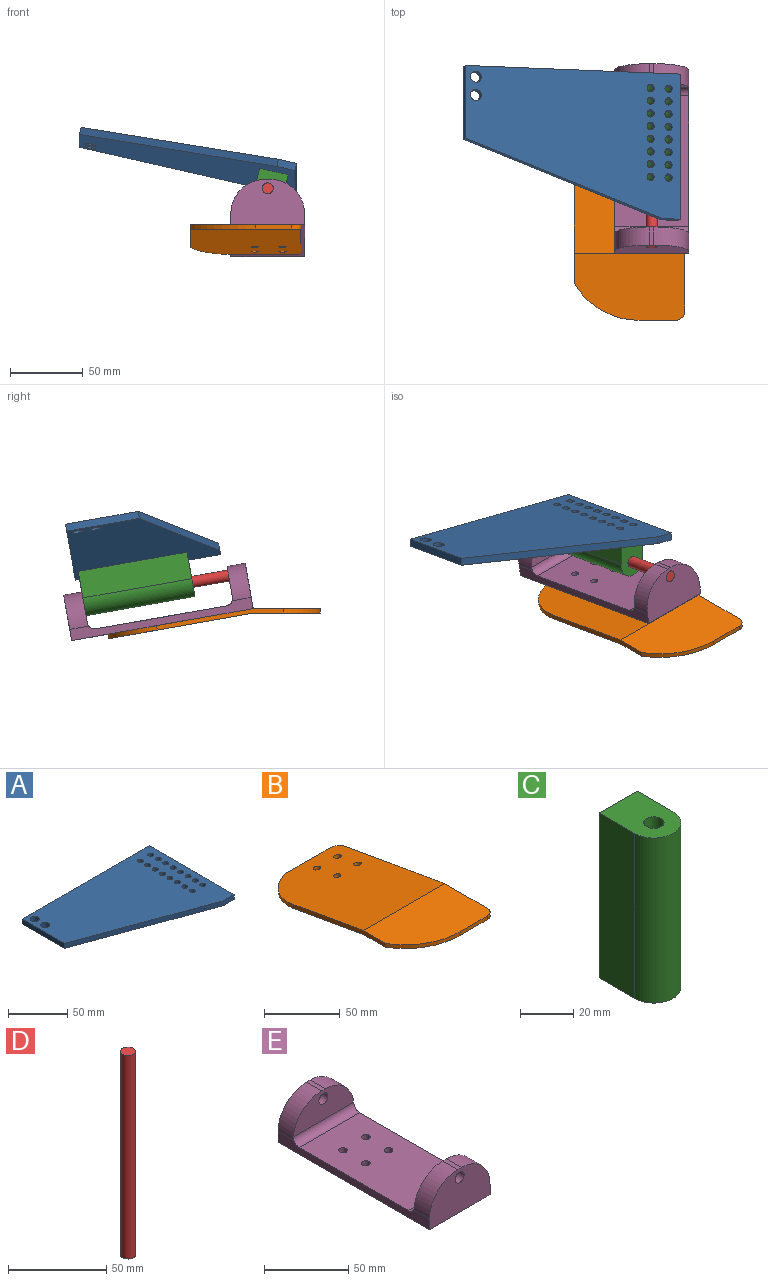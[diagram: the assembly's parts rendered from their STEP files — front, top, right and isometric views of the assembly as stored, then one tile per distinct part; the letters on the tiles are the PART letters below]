
ASSEMBLY  parts=5 mates=8
PART A: 25 faces, bbox 152.4x101.6x5.1 mm
  f0: plane 101.6x5.08mm, normal (1,0,0), area 516.1mm2, adj f1,f20,f22,f23
  f1: plane 152.4x5.08mm, normal (0,1,0), area 774.2mm2, adj f0,f2,f22,f23
  f2: plane 50.8x5.08mm, normal (-1,0,0), area 258.1mm2, adj f1,f22,f23,f24
  f3: cylinder r=3.81mm len=7.62mm, axis (0,0,-1), area 121.6mm2, adj f22,f23
  f4: cylinder r=2.54mm len=5.08mm, axis (0,0,-1), area 81.1mm2, adj f22,f23
  f5: cylinder r=2.54mm len=5.08mm, axis (0,0,-1), area 81.1mm2, adj f22,f23
  f6: cylinder r=2.54mm len=5.08mm, axis (0,0,-1), area 81.1mm2, adj f22,f23
  f7: cylinder r=2.54mm len=5.08mm, axis (0,0,-1), area 81.1mm2, adj f22,f23
  f8: cylinder r=2.54mm len=5.08mm, axis (0,0,-1), area 81.1mm2, adj f22,f23
  f9: cylinder r=2.54mm len=5.08mm, axis (0,0,-1), area 81.1mm2, adj f22,f23
  f10: cylinder r=2.54mm len=5.08mm, axis (0,0,-1), area 81.1mm2, adj f22,f23
  f11: cylinder r=2.54mm len=5.08mm, axis (0,0,-1), area 81.1mm2, adj f22,f23
  f12: cylinder r=2.54mm len=5.08mm, axis (0,0,-1), area 81.1mm2, adj f22,f23
  f13: cylinder r=2.54mm len=5.08mm, axis (0,0,-1), area 81.1mm2, adj f22,f23
  f14: cylinder r=2.54mm len=5.08mm, axis (0,0,-1), area 81.1mm2, adj f22,f23
  f15: cylinder r=2.54mm len=5.08mm, axis (0,0,-1), area 81.1mm2, adj f22,f23
  f16: cylinder r=2.54mm len=5.08mm, axis (0,0,-1), area 81.1mm2, adj f22,f23
  f17: cylinder r=2.54mm len=5.08mm, axis (0,0,-1), area 81.1mm2, adj f22,f23
  f18: cylinder r=2.54mm len=5.08mm, axis (0,0,-1), area 81.1mm2, adj f22,f23
  f19: cylinder r=2.54mm len=5.08mm, axis (0,0,-1), area 81.1mm2, adj f22,f23
  f20: plane 12.83x5.08mm, normal (0,-1,0), area 65.2mm2, adj f0,f22,f23,f24
  f21: cylinder r=3.81mm len=7.62mm, axis (0,0,-1), area 121.6mm2, adj f22,f23
  f22: plane 152.4x101.6mm, normal (0,0,1), area 11523.2mm2, adj f0,f1,f2,f3,f4,f5,f6,f7
  f23: plane 152.4x101.6mm, normal (0,0,-1), area 11523.2mm2, adj f0,f1,f2,f3,f4,f5,f6,f7
  f24: plane 139.57x50.8mm, normal (-0.34,-0.94,0), area 754.5mm2, adj f2,f20,f22,f23
PART B: 16 faces, bbox 76.2x146.3x20.7 mm
  f0: plane 42.15x3.05mm, normal (0,0.98,-0.17), area 130.4mm2, adj f1,f2,f13,f14
  f1: plane 100.06x76.2mm, normal (0,-0.17,-0.98), area 7396.1mm2, adj f0,f3,f4,f8,f9,f10,f11,f12
  f2: plane 100.06x76.2mm, normal (0,0.17,0.98), area 7396.1mm2, adj f0,f3,f4,f7,f9,f10,f11,f12
  f3: plane 133.71x19.59mm, normal (1,0,0), area 415.6mm2, adj f1,f2,f7,f8,f14,f15
  f4: plane 87.48x14.8mm, normal (-1,0,0), area 272.1mm2, adj f1,f2,f5,f7,f8,f13
  f5: cylinder r=51.88mm len=44.61mm, axis (0,0,-1), area 163.7mm2, adj f4,f6,f7,f8
  f6: plane 25.24x3.05mm, normal (0,-1,0), area 76.9mm2, adj f5,f7,f8,f15
  f7: plane 76.2x46.26mm, normal (0,0,1), area 3185.4mm2, adj f2,f3,f4,f5,f6,f15
  f8: plane 76.2x45.72mm, normal (0,0,-1), area 3144.4mm2, adj f1,f3,f4,f5,f6,f15
  f9: cylinder r=2.54mm len=5.54mm, axis (0,0.17,0.98), area 49.4mm2, adj f1,f2
  f10: cylinder r=2.54mm len=5.54mm, axis (0,0.17,0.98), area 49.4mm2, adj f1,f2
  f11: cylinder r=2.54mm len=5.54mm, axis (0,0.17,0.98), area 49.4mm2, adj f1,f2
  f12: cylinder r=2.54mm len=5.54mm, axis (0,0.17,0.98), area 49.4mm2, adj f1,f2
  f13: cylinder r=37.02mm len=33.97mm, axis (0,0.17,0.98), area 145.1mm2, adj f0,f1,f2,f4
  f14: cylinder r=6.35mm len=6.79mm, axis (0,-0.17,-0.98), area 30.9mm2, adj f0,f1,f2,f3
  f15: cylinder r=6.35mm len=6.35mm, axis (0,0,-1), area 30.4mm2, adj f3,f6,f7,f8
PART C: 39 faces, bbox 20.3x29.2x76.2 mm
  f0: plane 76.2x19.05mm, normal (-1,0,0), area 1451.6mm2, adj f1,f3,f5,f6
  f1: cylinder r=10.16mm len=76.2mm, axis (0,0,-1), area 2432.2mm2, adj f0,f2,f5,f6
  f2: plane 76.2x19.05mm, normal (1,0,0), area 1451.6mm2, adj f1,f3,f5,f6
  f3: plane 76.2x20.32mm, normal (0,1,0), area 1224.1mm2, adj f0,f2,f5,f6,f7,f9,f11,f13
  f4: cylinder r=3.81mm len=76.2mm, axis (0,0,-1), area 1824.1mm2, adj f5,f6
  f5: plane 29.21x20.32mm, normal (0,0,1), area 503.6mm2, adj f0,f1,f2,f3,f4
  f6: plane 29.21x20.32mm, normal (0,0,-1), area 503.6mm2, adj f0,f1,f2,f3,f4
  f7: cylinder r=2.54mm len=12.7mm, axis (0,1,0), area 202.7mm2, adj f3,f8
  f8: plane 5.08x5.08mm, normal (0,1,0), area 20.3mm2, adj f7
  f9: cylinder r=2.54mm len=12.7mm, axis (0,1,0), area 202.7mm2, adj f3,f10
  f10: plane 5.08x5.08mm, normal (0,1,0), area 20.3mm2, adj f9
  f11: cylinder r=2.54mm len=12.7mm, axis (0,1,0), area 202.7mm2, adj f3,f12
  f12: plane 5.08x5.08mm, normal (0,1,0), area 20.3mm2, adj f11
  f13: cylinder r=2.54mm len=12.7mm, axis (0,1,0), area 202.7mm2, adj f3,f14
  f14: plane 5.08x5.08mm, normal (0,1,0), area 20.3mm2, adj f13
  f15: cylinder r=2.54mm len=12.7mm, axis (0,1,0), area 202.7mm2, adj f3,f16
  f16: plane 5.08x5.08mm, normal (0,1,0), area 20.3mm2, adj f15
  f17: cylinder r=2.54mm len=12.7mm, axis (0,1,0), area 202.7mm2, adj f3,f18
  f18: plane 5.08x5.08mm, normal (0,1,0), area 20.3mm2, adj f17
  f19: cylinder r=2.54mm len=12.7mm, axis (0,1,0), area 202.7mm2, adj f3,f20
  f20: plane 5.08x5.08mm, normal (0,1,0), area 20.3mm2, adj f19
  f21: cylinder r=2.54mm len=12.7mm, axis (0,1,0), area 202.7mm2, adj f3,f22
  f22: plane 5.08x5.08mm, normal (0,1,0), area 20.3mm2, adj f21
  f23: cylinder r=2.54mm len=12.7mm, axis (0,1,0), area 202.7mm2, adj f3,f24
  f24: plane 5.08x5.08mm, normal (0,1,0), area 20.3mm2, adj f23
  f25: cylinder r=2.54mm len=12.7mm, axis (0,1,0), area 202.7mm2, adj f3,f26
  f26: plane 5.08x5.08mm, normal (0,1,0), area 20.3mm2, adj f25
  f27: cylinder r=2.54mm len=12.7mm, axis (0,1,0), area 202.7mm2, adj f3,f28
  f28: plane 5.08x5.08mm, normal (0,1,0), area 20.3mm2, adj f27
  f29: cylinder r=2.54mm len=12.7mm, axis (0,1,0), area 202.7mm2, adj f3,f30
  f30: plane 5.08x5.08mm, normal (0,1,0), area 20.3mm2, adj f29
  f31: cylinder r=2.54mm len=12.7mm, axis (0,1,0), area 202.7mm2, adj f3,f32
  f32: plane 5.08x5.08mm, normal (0,1,0), area 20.3mm2, adj f31
  f33: cylinder r=2.54mm len=12.7mm, axis (0,1,0), area 202.7mm2, adj f3,f34
  f34: plane 5.08x5.08mm, normal (0,1,0), area 20.3mm2, adj f33
  f35: cylinder r=2.54mm len=12.7mm, axis (0,1,0), area 202.7mm2, adj f3,f36
  f36: plane 5.08x5.08mm, normal (0,1,0), area 20.3mm2, adj f35
  f37: cylinder r=2.54mm len=12.7mm, axis (0,1,0), area 202.7mm2, adj f3,f38
  f38: plane 5.08x5.08mm, normal (0,1,0), area 20.3mm2, adj f37
PART D: 3 faces, bbox 7.6x7.6x127 mm
  f0: cylinder r=3.81mm len=127mm, axis (0,0,-1), area 3040.2mm2, adj f1,f2
  f1: plane 7.62x7.62mm, normal (0,0,1), area 45.6mm2, adj f0
  f2: plane 7.62x7.62mm, normal (0,0,-1), area 45.6mm2, adj f0
PART E: 22 faces, bbox 50.8x127x31.8 mm
  f0: plane 127x7.84mm, normal (-1,0,0), area 725.4mm2, adj f6,f7,f9,f12,f16,f18,f20,f21
  f1: cylinder r=2.54mm len=5.08mm, axis (0,0,-1), area 81.1mm2, adj f6,f7
  f2: cylinder r=2.54mm len=5.08mm, axis (0,0,-1), area 81.1mm2, adj f6,f7
  f3: cylinder r=2.54mm len=5.08mm, axis (0,0,-1), area 81.1mm2, adj f6,f7
  f4: plane 127x7.84mm, normal (1,0,0), area 725.4mm2, adj f6,f7,f9,f12,f17,f19,f20,f21
  f5: cylinder r=2.54mm len=5.08mm, axis (0,0,-1), area 81.1mm2, adj f6,f7
  f6: plane 91.44x50.8mm, normal (0,0,1), area 4564.1mm2, adj f0,f1,f2,f3,f4,f5,f20,f21
  f7: plane 127x50.8mm, normal (0,0,-1), area 6370.5mm2, adj f0,f1,f2,f3,f4,f5,f9,f12
  f8: plane 50.57x21.59mm, normal (0,-1,0), area 805.9mm2, adj f10,f15,f18,f19,f21
  f9: plane 50.8x31.75mm, normal (0,1,0), area 1321.8mm2, adj f0,f4,f7,f10,f15,f18,f19
  f10: plane 12.7x2.97mm, normal (0,0,1), area 37.7mm2, adj f8,f9,f18,f19
  f11: plane 50.57x21.59mm, normal (0,1,0), area 805.9mm2, adj f13,f14,f16,f17,f20
  f12: plane 50.8x31.75mm, normal (0,-1,0), area 1321.8mm2, adj f0,f4,f7,f13,f14,f16,f17
  f13: plane 12.7x2.97mm, normal (0,0,1), area 37.7mm2, adj f11,f12,f16,f17
  f14: cylinder r=3.81mm len=12.7mm, axis (0,-1,0), area 304mm2, adj f11,f12
  f15: cylinder r=3.81mm len=12.7mm, axis (0,-1,0), area 304mm2, adj f8,f9
  f16: cylinder r=23.92mm len=23.92mm, axis (0,1,0), area 477.5mm2, adj f0,f11,f12,f13,f20
  f17: cylinder r=23.92mm len=23.92mm, axis (0,-1,0), area 477.5mm2, adj f4,f11,f12,f13,f20
  f18: cylinder r=23.92mm len=23.92mm, axis (0,1,0), area 477.5mm2, adj f0,f8,f9,f10,f21
  f19: cylinder r=23.92mm len=23.92mm, axis (0,-1,0), area 477.5mm2, adj f4,f8,f9,f10,f21
  f20: cylinder r=5.08mm len=50.8mm, axis (-1,0,0), area 405.1mm2, adj f0,f4,f6,f11,f16,f17
  f21: cylinder r=5.08mm len=50.8mm, axis (1,0,0), area 405.1mm2, adj f0,f4,f6,f8,f18,f19
PLACE A rot(axis=(-0.61,0.79,-0.07),16.4deg) t=(-51.82,44.85,60.1)mm
PLACE B t=(-1.03,-26.06,11.74)mm fixed
PLACE C rot(axis=(0.98,0.11,-0.13),80.9deg) t=(3.69,86.37,19.96)mm
PLACE D rot(axis=(-0.99,0.11,0.09),100.6deg) t=(3.69,-26.19,39.81)mm
PLACE E rot(axis=(-1,0,0),10deg) t=(3.69,31.93,3.76)mm
MATE fastened B.f10 <-> E.f5  axis (0,0.17,0.98) through (13.85,38.18,2.66)mm
MATE planar E.f8 <-> C.f6  axis (0,-0.98,0.17) through (3.69,85.27,13.69)mm
MATE planar B.f2 <-> E.f7  axis (0,0.17,0.98) through (-10.7,17.6,6.29)mm
MATE planar C.f11 <-> A.f21  axis (0.22,0.17,0.96) through (14.15,64.33,41.25)mm
MATE slider D.f0 <-> C.f1  axis (0,-0.98,0.17) through (3.69,-26.19,39.81)mm
MATE fastened C.f17 <-> A.f18  axis (0.22,0.17,0.96) through (14.15,73.09,39.7)mm
MATE revolute E.f14 <-> D.f0  axis (0,0.98,-0.17) through (3.69,98.88,17.75)mm
MATE planar E.f14 <-> D.f0  axis (0,0.98,-0.17) through (3.69,98.88,17.75)mm
